# Revit family: NBS_HeatraeSadia_StrgWtrHtrsElctrc_SupremeSS
name_source: partatom
category: Plumbing Fixtures
revit_build: Autodesk Revit 2014 (Build: 20130709_2115(x64)
units: mm (PartAtom-declared; Revit-internal decimal feet)

## types (3) — shared parameters
Arrangement = Single point – mains supply
AssetType = Fixed
CW Connection = Yes
CasingFinish = Stainless steel
Color = Natural
Connections = Bottom or rear entry is possible using 15 mm push-fit connections
Controls = Satin chrome finished heavy duty die-cast push/ pull lever
Description = Water boiling heater
DurationUnit = year
Features = Intelliboil™Plus technology, integral electronic water conditioner, power 'on’ indicator, ‘ready’ indicator, detachable steam condensing chamber
Fixing = Wall fixed
FlowRate = To suit draw off requirements
HW Connection = No
HeatTransferSurfaceArea = 0
IPCode = IPX2
IfcExportAs = IfcBoilerType
IfcExportType = WATER
IsWaterStorageHeater = Yes
ManufacturerName = Heatrae Sadia
ManufacturerURL = www.heatraesadia.com
Material = Outer casing: Fingerprint-resistant stainless steel with grey ABS mouldings; Water container: Moulded polyphenylene sulphide; Heat unit: Low watt density Superloy element
NBSCertification = http://www.nationalbimlibrary.com
NBSDescription = Storage water heaters, electric
NBSReference = 90-15-35/440
NominalWidth = 337 mm  [stored 1.10564 ft]
OutletTemperatureRange = 100
PartialLoadEfficiencyCurves = 0
PressureRating = 0
ProductInformation = www.heatraesadia.com/docs/Drinking_water_brochure.pdf
Rating = 2.5 kW
SafetyFeatures = Low pressure vented, dry start protection by self-resetting bi-metal thermal cut-out, boil-dry protection by manually-resettable disc-type bi-metal cut-out
StorageWaterHeaterMaterial = NBS_Concept
ThermalInsulation = CFC/HCFC free (ODP zero) pre-moulded polystyrene and thermoplastic blend
ThirdPartyCertification = BEAB approved
Uniclass2 = 90-90-46/428
Uniclass2015Description = Electric storage water heaters
Uniclass2015Reference = Pr_60_60_96_28
Uniclass2015Version = Products v1.1
Vent Connection = Yes
Version = 1
WarrantyDurationParts = 2
WarrantyDurationUnit = year
WarrantyStartDate = 1900-12-31T23:59:59
Waste Connection = No
WaterInletTemperatureRange = 0
Width = 337 mm  [stored 1.10564 ft]
zero-valued in all types: HeatOutput, NominalEfficiency, NominalEnergyConsumption, NominalPartLoadRatio

## per-type parameters (varying)
| type | Accessories | BIMObjectName | BodyHeight | CableEntry | Depth | Height | InletPlacement | ModelNumber | ModelReference | Name | NominalHeight | NominalLength | OutletPlacement | Size | VentPlacement | WaterStorageCapacity | Weight |
| Supreme150SS | Counter stand (95:970:132), Drip tray no waste (95:970:128), Drip tray with waste (95:970:123), Programmable timer (95:970:124), Water filter system (95:970:129) | NBS_HeatraeSadia_StorageWaterHeatersElectric_Supreme150SS | 383.6 mm  [stored 1.25853 ft] | 111 mm | 203 mm  [stored 0.66601 ft] | 423 mm  [stored 1.3878 ft] | 80 mm  [stored 0.262467 ft] | 95:200:240 | Supreme 150SS | StorageWaterHeatersElectric_Supreme150SS_HeatraeSadia | 423 mm  [stored 1.3878 ft] | 203 mm  [stored 0.66601 ft] | 160 mm  [stored 0.524934 ft] | 423 x 337 x 203 mm | 112 mm  [stored 0.367454 ft] | 2.5 | 12 |
| Supreme165SS | Counter stand (95:970:133), Drip tray no waste (95:970:128), Drip tray with waste (95:970:123), Programmable timer (95:970:124), Water filter system (95:970:129) | NBS_HeatraeSadia_StorageWaterHeatersElectric_Supreme165SS | 466 mm  [stored 1.52887 ft] | 101 mm  [stored 0.331365 ft] | 203 mm  [stored 0.66601 ft] | 501 mm  [stored 1.6437 ft] | 101 mm  [stored 0.331365 ft] | 95:200:241 | Supreme 165SS | StorageWaterHeatersElectric_Supreme165SS_HeatraeSadia | 501 mm  [stored 1.6437 ft] | 203 mm  [stored 0.66601 ft] | 160 mm  [stored 0.524934 ft] | 501 x 337 x 203 mm | 133 mm  [stored 0.436352 ft] | 5 | 16 |
| Supreme180SS | Counter stand (95:970:133), Drip tray no waste (95:970:128), Drip tray with waste (95:970:123), Programmable timer (95:970:124), Water filter system (95:970:129) | NBS_HeatraeSadia_StorageWaterHeatersElectric_Supreme180SS | 471 mm  [stored 1.54528 ft] | 101 mm  [stored 0.331365 ft] | 262 mm  [stored 0.85958 ft] | 506 mm  [stored 1.6601 ft] | 101 mm  [stored 0.331365 ft] | 95:200:242 | Supreme 180SS | StorageWaterHeatersElectric_Supreme180SS_HeatraeSadia | 506 mm  [stored 1.6601 ft] | 262 mm  [stored 0.85958 ft] | 220 mm  [stored 0.721785 ft] | 506 x 337 x 262 mm | 133 mm  [stored 0.436352 ft] | 7.5 | 21 |

note: [stored X ft] marks values corroborated as IEEE doubles in the binary element streams (Revit-internal decimal feet)

## geometry (parser evidence)
native form markers: Sweep x3
no freeform markers — native parametric forms only
